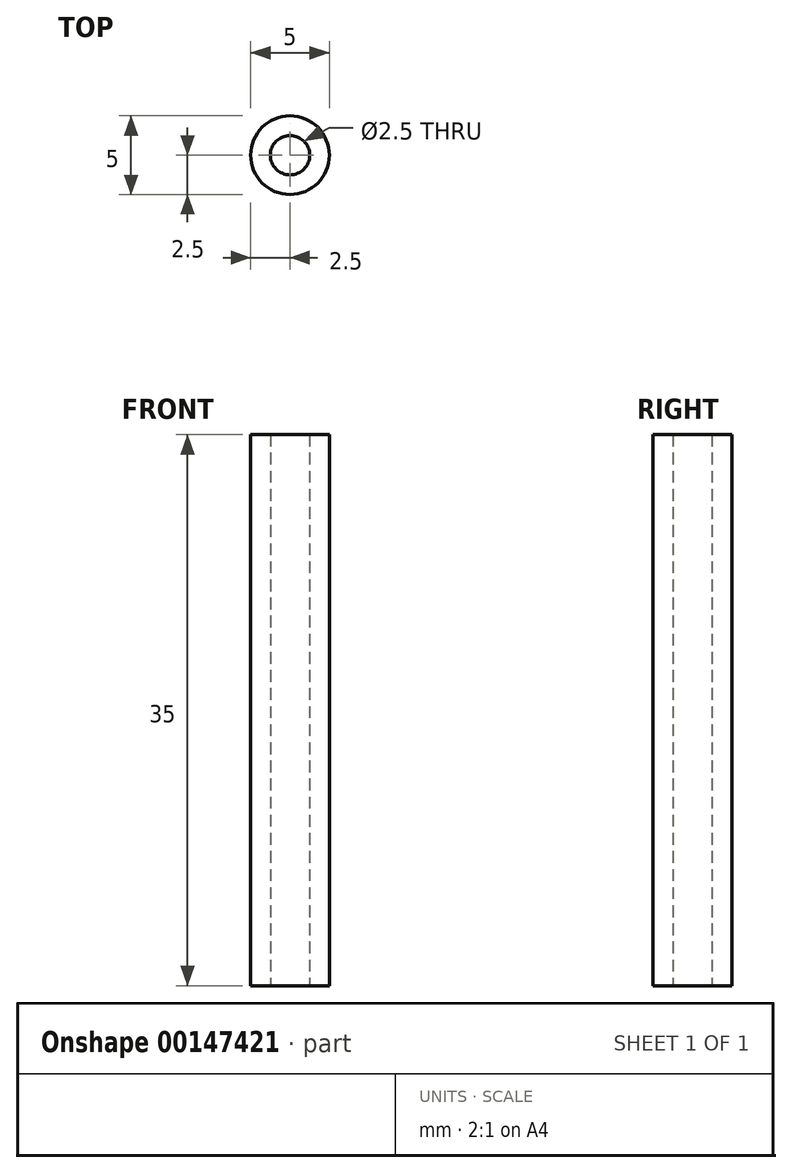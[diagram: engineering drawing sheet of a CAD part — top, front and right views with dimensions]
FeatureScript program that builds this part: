
annotation { "Feature Type Name" : "Feature", "Feature Type Description" : "" }
export const myFeature = defineFeature(function(context is Context, id is Id, definition is map)
    precondition{}
    {
        {
            var Q0;
            Q0=qCreatedBy(makeId("Top.planeOp"),FACE);
            var sketch = newSketch(context, id + "F0", { "sketchPlane" : qUnion([Q0])});
            skCircle(sketch, "E0", {"center": v(0, 0) * mm, "radius": 2.5 * mm});
            skCircle(sketch, "E1", {"center": v(0, 0) * mm, "radius": 1.25 * mm});
            skSolve(sketch);
        }
        {
            var Q0;
            Q0=qSketchRegion(id+"F0",true);
            extrude(context, id + "F1", {"entities" : qUnion([Q0]), "depth" : 35 * mm});
        }
    });
